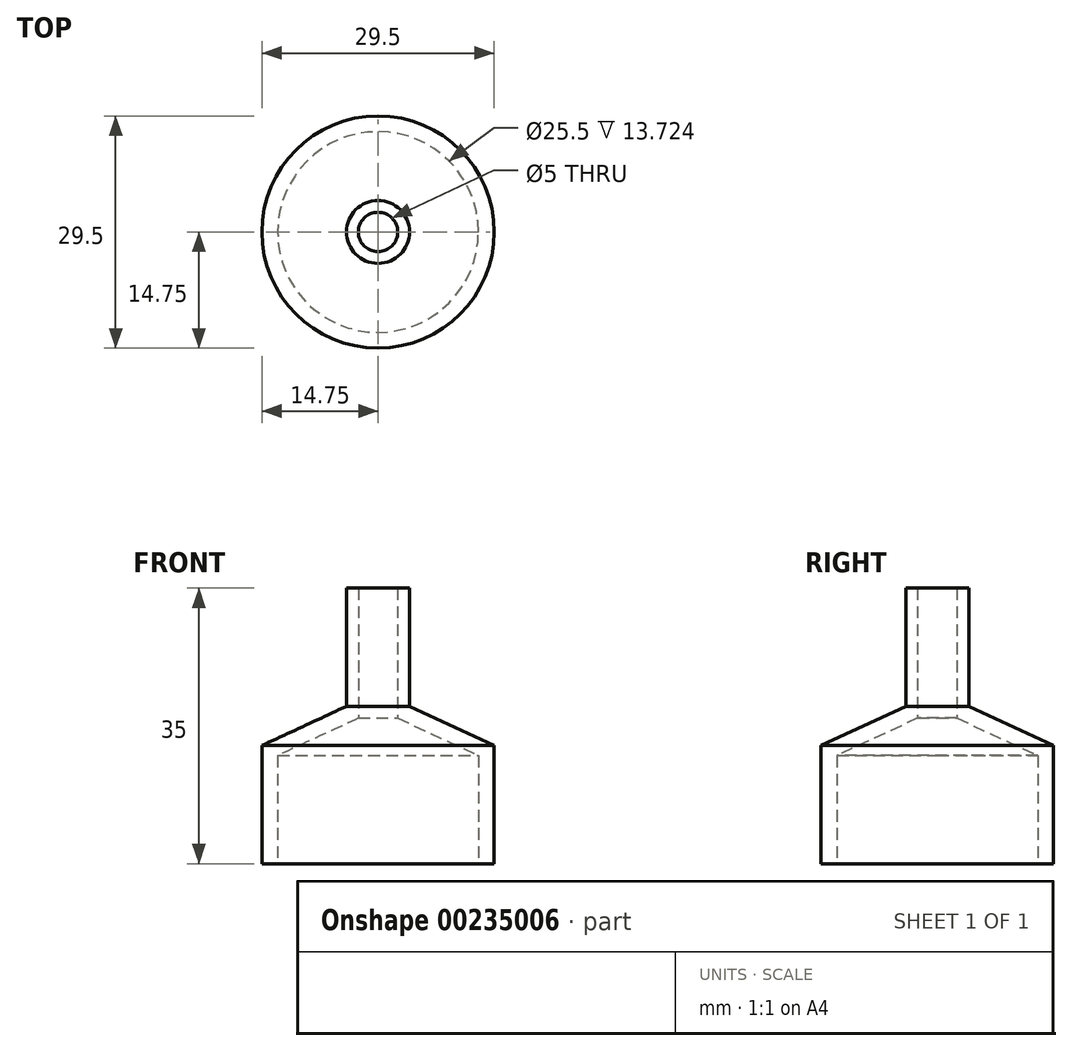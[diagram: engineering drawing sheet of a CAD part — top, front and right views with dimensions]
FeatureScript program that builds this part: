
annotation { "Feature Type Name" : "Feature", "Feature Type Description" : "" }
export const myFeature = defineFeature(function(context is Context, id is Id, definition is map)
    precondition{}
    {
        {
            var Q0;
            Q0=qCreatedBy(makeId("Right.planeOp"),FACE);
            var sketch = newSketch(context, id + "F0", { "sketchPlane" : qUnion([Q0])});
            skLineSegment(sketch, "E0", {"start": v(12.75, 0) * mm, "end": v(14.75, 0) * mm});
            skLineSegment(sketch, "E1", {"start": v(14.75, 0) * mm, "end": v(14.75, 15) * mm});
            skLineSegment(sketch, "E2", {"start": v(14.75, 15) * mm, "end": v(4, 20) * mm});
            skLineSegment(sketch, "E3", {"start": v(4, 20) * mm, "end": v(4, 35) * mm});
            skLineSegment(sketch, "E4", {"start": v(4, 35) * mm, "end": v(2.5, 35) * mm});
            skLineSegment(sketch, "E5", {"start": v(2.5, 35) * mm, "end": v(2.5, 18.5) * mm});
            skLineSegment(sketch, "E6", {"start": v(2.5, 18.5) * mm, "end": v(12.75, 13.72) * mm});
            skLineSegment(sketch, "E7", {"start": v(12.75, 13.72) * mm, "end": v(12.75, 0) * mm});
            skLineSegment(sketch, "E8", {"start": v(0, 0) * mm, "end": v(0, 13.85) * mm, "construction": true});
            skSolve(sketch);
        }
        {
            var Q0;
            Q0=qSketchRegion(id+"F0",true);
            var Q1;
            Q1=sQuery(id+"F0.wireOp",EDGE,"E8");
            revolve(context, id + "F1", {"entities" : qUnion([Q0]), "axis" : qUnion([Q1]), "revolveType" : RevolveType.FULL});
        }
    });
